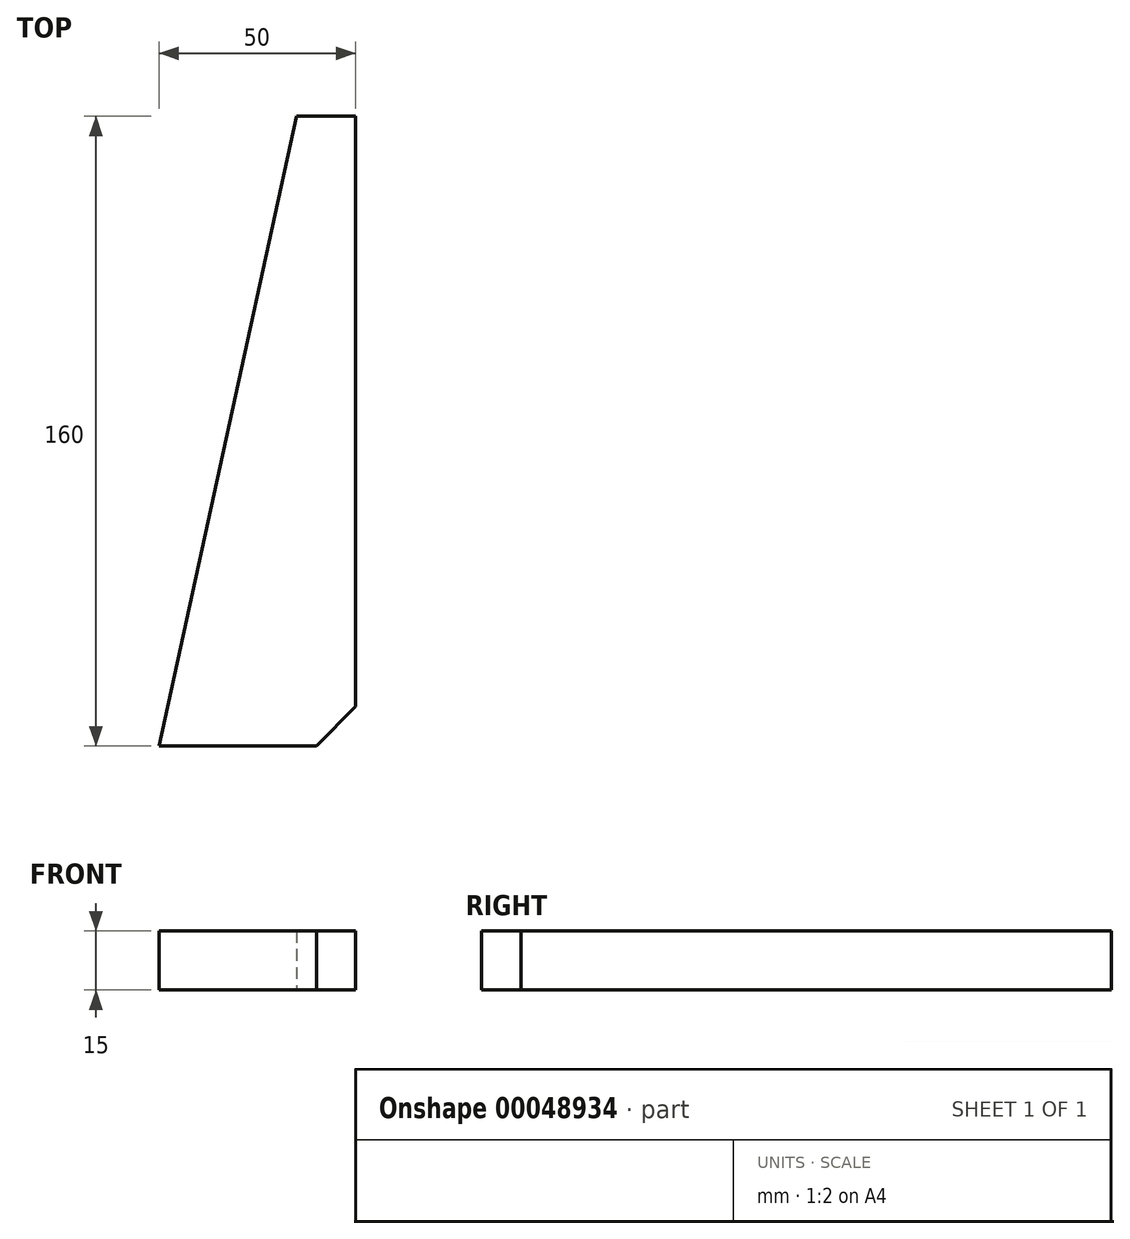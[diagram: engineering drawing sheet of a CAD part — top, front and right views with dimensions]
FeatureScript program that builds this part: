
annotation { "Feature Type Name" : "Feature", "Feature Type Description" : "" }
export const myFeature = defineFeature(function(context is Context, id is Id, definition is map)
    precondition{}
    {
        {
            var Q0;
            Q0=qCreatedBy(makeId("Top.planeOp"),FACE);
            var sketch = newSketch(context, id + "F0", { "sketchPlane" : qUnion([Q0])});
            skLineSegment(sketch, "E0", {"start": v(0, 0) * mm, "end": v(50, 0) * mm});
            skLineSegment(sketch, "E1", {"start": v(50, 0) * mm, "end": v(50, 160) * mm});
            skLineSegment(sketch, "E2", {"start": v(50, 160) * mm, "end": v(35, 160) * mm});
            skLineSegment(sketch, "E3", {"start": v(35, 160) * mm, "end": v(0, 0) * mm});
            skSolve(sketch);
        }
        {
            var Q0;
            Q0 = qSketchRegion(id + "F0", true);
            extrude(context, id + "F1", {"entities" : qUnion([Q0]), "depth" : 15 * mm});
        }
        {
            var Q0;
            Q0=makeQuery(id+"F1.opExtrude","SWEPT_EDGE",EDGE,{"disambiguationData":[OSD([sQuery(id+"F0.wireOp",EDGE,"E0"),sQuery(id+"F0.wireOp",EDGE,"E1")])]});
            chamfer(context, id + "F2", {"entities" : qUnion([Q0]), "chamferType" : ChamferType.OFFSET_ANGLE, "width" : 10 * mm, "oppositeDirection" : false, "angle" : 45 * degree, "tangentPropagation" : true});
        }
    });
